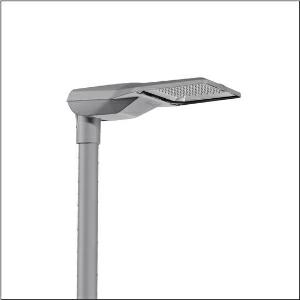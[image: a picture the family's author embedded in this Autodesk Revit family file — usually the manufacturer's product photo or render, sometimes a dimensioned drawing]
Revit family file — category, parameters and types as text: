
# Revit family: streetlight_sl_21_midi___st0_8a_5xe7c23a08lb_df95
name_source: partatom
category: Lighting Fixtures
units: mm (PartAtom-declared; Revit-internal decimal feet)

## family parameters
Cut with Voids When Loaded = No
Host = Face
Light Source = No
Part Type = Normal
Room Calculation Point = No
Round Connector Dimension = Use Diameter
Shared = No

## types (1)
- --- (1 x LED, 11880 lm, 98.3 W, 2200K)
    Apparent Load = 98 VA
    CIE Flux Codes = 38 75 97 100 100
    Color Rendering = 70
    Color Temperature = 2200K
    Default Elevation = 1800 mm
    Description = Streetlight SL 21 midi, mast luminaire, primary light control with lens, of PMMA, primary optical cover: cover, of toughened safety glass, transparent, light distribution: ST0.8a, light emission: direct distribution, primary light characteristic: asymmetric, installation type: post-top, side-entry, LED, 3G 1.5mm², High Power LED, rated luminous flux: 11.880lm, luminous efficacy: 121lm/W, light colour: 722, colour temperature: 2200K, control: overheat protection, constant luminous flux control, time-dependent luminous flux control, flexible luminous flux parameterisation, mains connection: 220..240V, AC, 50/60Hz, connection cable pre-assembled, cable length: 10,5m, wiring characteristics: H07RN-F, start of lifetime: 98W, end of service life: 101W, reduction: 44W, luminaire housing, of diecast aluminium, powder-coated, Siteco® metallic grey (DB 702S), corrosivity category C5 mid according to DIN EN ISO 12944, please order mast flange separately, inclination adjustable: 0°, 5°, 10°, 15°, sealing non-destructively replaceable, multi-level sealing system, length: 644mm, width: 335mm, height: 110mm, mast flange for spigot size: 42mm (side-entry): 5XC10008XM4, 60/48mm (side-entry/post-top): 5XC10108XM2, 76/60mm (side-entry/post-top): 5XC10108XM1, protection rating (complete): IP66, insulation class (complete): insulation class II (safety insulation), certification: CE, ENEC, ENEC+, VDE, impact resistance: IK09, permissible operating ambient temperature for outdoor applications: -40..+50°C, standard-compliant lighting for roads and squares, packaging unit: 1 piece

Light Distribution: ST0.8a
    Height = 111 mm
    Lamp = 1 x LED
    Lamp Light Flux = 11880 lm
    Lamp Power = 98.3 W
    Lamp count = 1
    Length = 644 mm
    Luminous efficacy = 121 lm/W
    Manufacturer = Siteco
    ModVariant = No
    Model = 5XE7C23A08LB
    Number of Poles = 1
    OnlyDefault = Yes
    Power Factor = 1
    Product Name = Streetlight SL 21 midi | ST0.8a
    Product group = mast luminaire | pylon top
    ProductGroupID = 6100
    Protection Class = Protection class II
    Protection Degree = IP 66
    RLX_Detail_Level = 1
    RLX_Emergency_Light_Flux = 0 lm
    RLX_Emergency_Type = 0
    RLX_Emergency_Type_DB = No
    RlxData = <blob elided: 90537 chars, md5=2d3ba2b7>
    Socket = socket
    Standby Power = 0 W
    System Light Flux = 11880 lm
    System Power = 98 W
    Type Comments = factory setting: luminous flux: 100 % | Output Level: 100 % | 1020 mA
    Type Image = l_1004298.jpg
    URL = http://relux.com
    VarID = @adj_137553
    Voltage = 0 V
    Weight = 0.00 kg
    Width = 336 mm

## geometry (parser evidence)
native form markers: Blend x4, Sweep x11
no freeform markers — native parametric forms only
